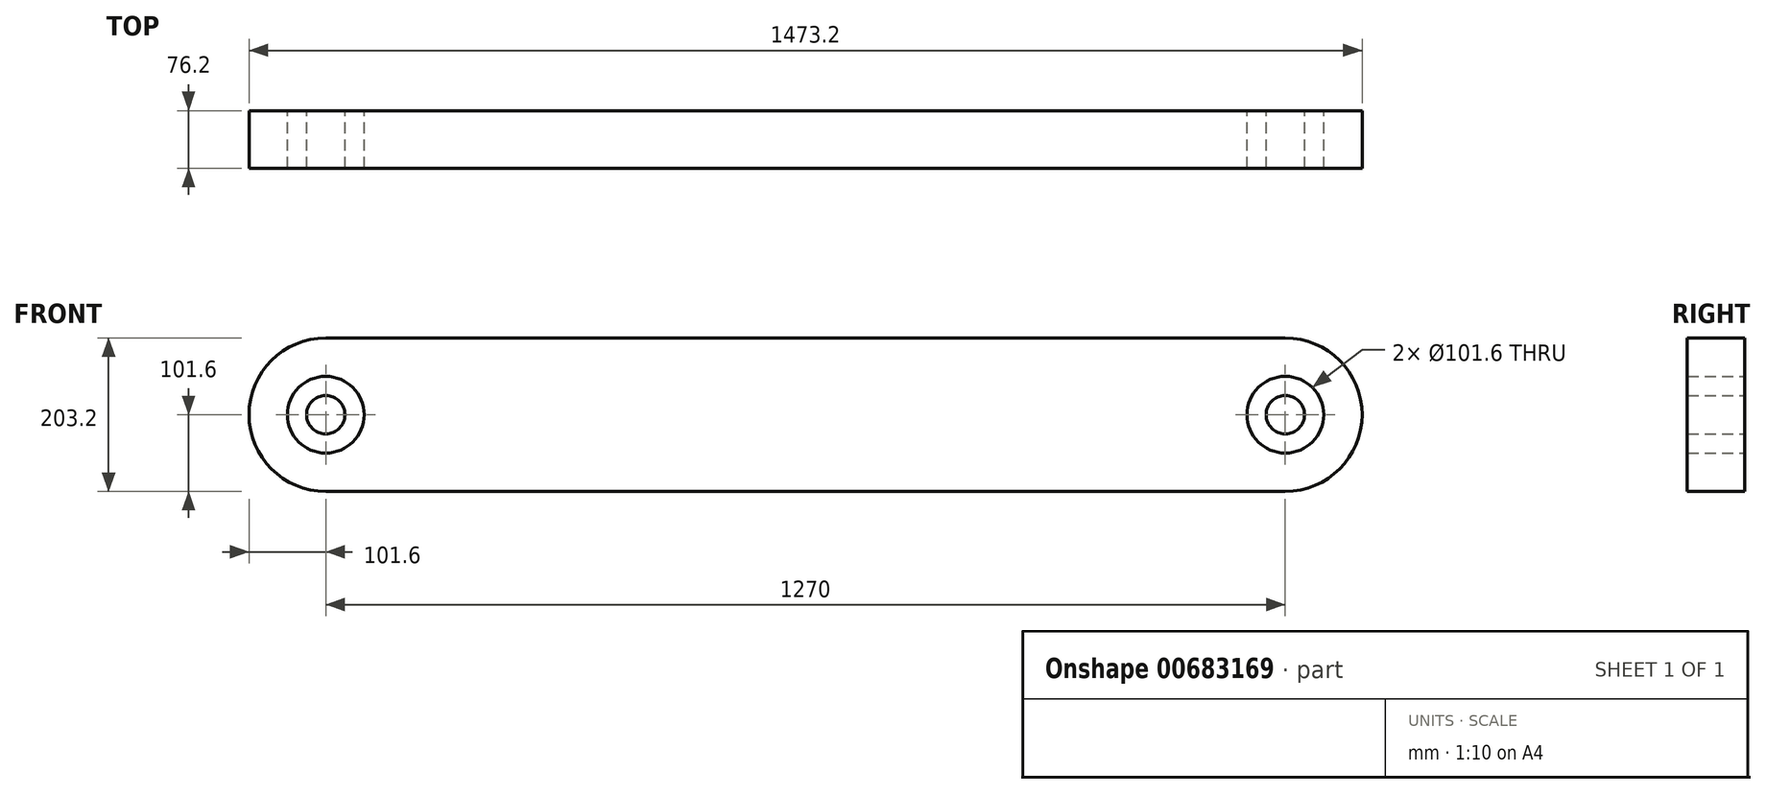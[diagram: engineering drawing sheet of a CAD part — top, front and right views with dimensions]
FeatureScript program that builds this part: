
annotation { "Feature Type Name" : "Feature", "Feature Type Description" : "" }
export const myFeature = defineFeature(function(context is Context, id is Id, definition is map)
    precondition{}
    {
        {
            var Q0;
            Q0=qCreatedBy(makeId("Front.planeOp"),FACE);
            var sketch = newSketch(context, id + "F0", { "sketchPlane" : qUnion([Q0])});
            skArc(sketch, "E0", {"start": v(0, 101.6) * mm, "mid": v(-101.6, 0) * mm, "end": v(0, -101.6) * mm});
            skArc(sketch, "E1", {"start": v(1270, -101.6) * mm, "mid": v(1371.6, 0) * mm, "end": v(1270, 101.6) * mm});
            skLineSegment(sketch, "E2", {"start": v(0, 101.6) * mm, "end": v(1270, 101.6) * mm});
            skLineSegment(sketch, "E3", {"start": v(0, -101.6) * mm, "end": v(1270, -101.6) * mm});
            skCircle(sketch, "E4", {"center": v(0, 0) * mm, "radius": 50.8 * mm});
            skCircle(sketch, "E5", {"center": v(1270, 0) * mm, "radius": 50.8 * mm});
            skCircle(sketch, "E6", {"center": v(0, 0) * mm, "radius": 25.4 * mm});
            skCircle(sketch, "E7", {"center": v(1270, 0) * mm, "radius": 25.4 * mm});
            skSolve(sketch);
        }
        {
            var Q0;
            Q0 = qSketchRegion(id + "F0", true);
            var Q1;
            Q1=makeQuery(id+"F0.imprint","IMPRINT",FACE,{"disambiguationData":[TD([[makeQuery(id+"F0.imprint","IMPRINT",EDGE,{"derivedFrom":sQuery(id+"F0.wireOp",EDGE,"E6")}),1.0]])]});
            var Q2;
            Q2=makeQuery(id+"F0.imprint","IMPRINT",FACE,{"disambiguationData":[TD([[makeQuery(id+"F0.imprint","IMPRINT",EDGE,{"derivedFrom":sQuery(id+"F0.wireOp",EDGE,"E7")}),1.0]])]});
            extrude(context, id + "F1", {"entities" : qUnion([Q0, Q1, Q2]), "depth" : 76.2 * mm, "offsetDistance" : 25.4 * mm});
        }
    });
